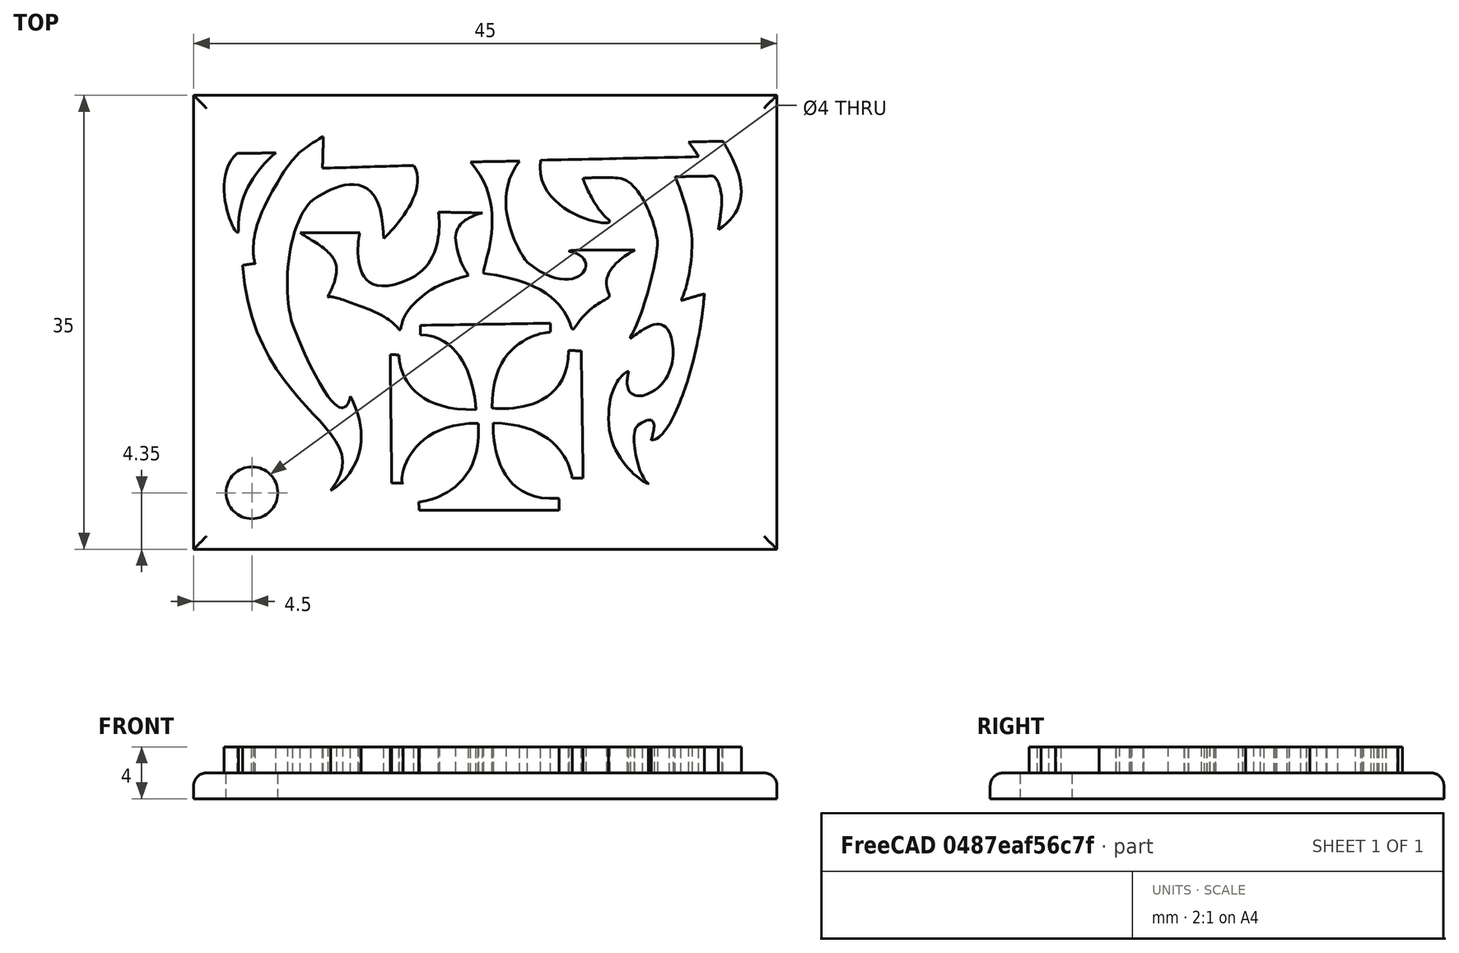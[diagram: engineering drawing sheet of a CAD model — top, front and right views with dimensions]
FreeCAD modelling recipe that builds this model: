
FCSTD DOCUMENT  (FreeCAD 0.14R3702 (Git))
Label: llaverocult
License: CC-BY 3.0
LicenseURL: http://creativecommons.org/licenses/by/3.0/
objects: Part::Feature×6, Part::Extrusion×6, Part::MultiFuse×2, Part::Box×1, Part::Fillet×1, Part::Cylinder×1, Part::Cut×1
note: 18 computed .brp shape members not serialized (recipe doc carries the construction recipe); baked Part::Feature solids carry a one-line shape summary decoded from their .brp

FEATURE [Part::Box] Box  label="Cubo"
  Height = 2
  Length = 45
  Placement = pos=(-22.5,-17.35,0) rot=(0,0,1;0rad)
  Width = 35
FEATURE [Part::Feature] path3048
  shape: bbox 13.96 x 27.27 x 2e-07 mm, 0 faces, 0 solids (baked)
FEATURE [Part::Feature] path3054
  shape: bbox 14.08 x 9.347 x 2e-07 mm, 0 faces, 0 solids (baked)
FEATURE [Part::Feature] path3075
  shape: bbox 12.68 x 13.83 x 2e-07 mm, 0 faces, 0 solids (baked)
FEATURE [Part::Feature] path2996
  shape: bbox 16.5 x 26.87 x 2e-07 mm, 0 faces, 0 solids (baked)
FEATURE [Part::Feature] path3000
  shape: bbox 4.594 x 6.678 x 2e-07 mm, 0 faces, 0 solids (baked)
FEATURE [Part::Feature] path5490
  shape: bbox 14.88 x 14.42 x 2e-07 mm, 0 faces, 0 solids (baked)
FEATURE [Part::Extrusion] Extrude
  Base = -> path3048
  Dir = (0,0,2)
  Solid = true
FEATURE [Part::Extrusion] Extrude001
  Base = -> path3054
  Dir = (0,0,2)
  Solid = true
FEATURE [Part::Extrusion] Extrude002
  Base = -> path3075
  Dir = (0,0,2)
  Solid = true
FEATURE [Part::Extrusion] Extrude003
  Base = -> path2996
  Dir = (0,0,2)
  Solid = true
FEATURE [Part::Extrusion] Extrude004
  Base = -> path3000
  Dir = (0,0,2)
  Solid = true
FEATURE [Part::Extrusion] Extrude005
  Base = -> path5490
  Dir = (0,0,2)
  Solid = true
FEATURE [Part::Fillet] Fillet
  Base = -> Box
  Edges = 4 edges r=1: [Edge2,Edge6,Edge10,Edge12]
  Placement = pos=(0,0,-1) rot=(0,0,1;0rad)
FEATURE [Part::MultiFuse] Fusion
  Placement = pos=(-1,1,1) rot=(0,0,1;0rad)
  Shapes = -> [Extrude004,Extrude002,Extrude,Extrude005,Extrude003,Extrude001]
FEATURE [Part::Cylinder] Cylinder  label="Cilindro"
  Angle = 360
  Height = 10
  Placement = pos=(-18,-13,-4) rot=(0,0,1;0rad)
  Radius = 2
FEATURE [Part::Cut] Cut
  Base = -> Fillet
  Tool = -> Cylinder
FEATURE [Part::MultiFuse] Fusion001
  Shapes = -> [Fusion,Cut]
